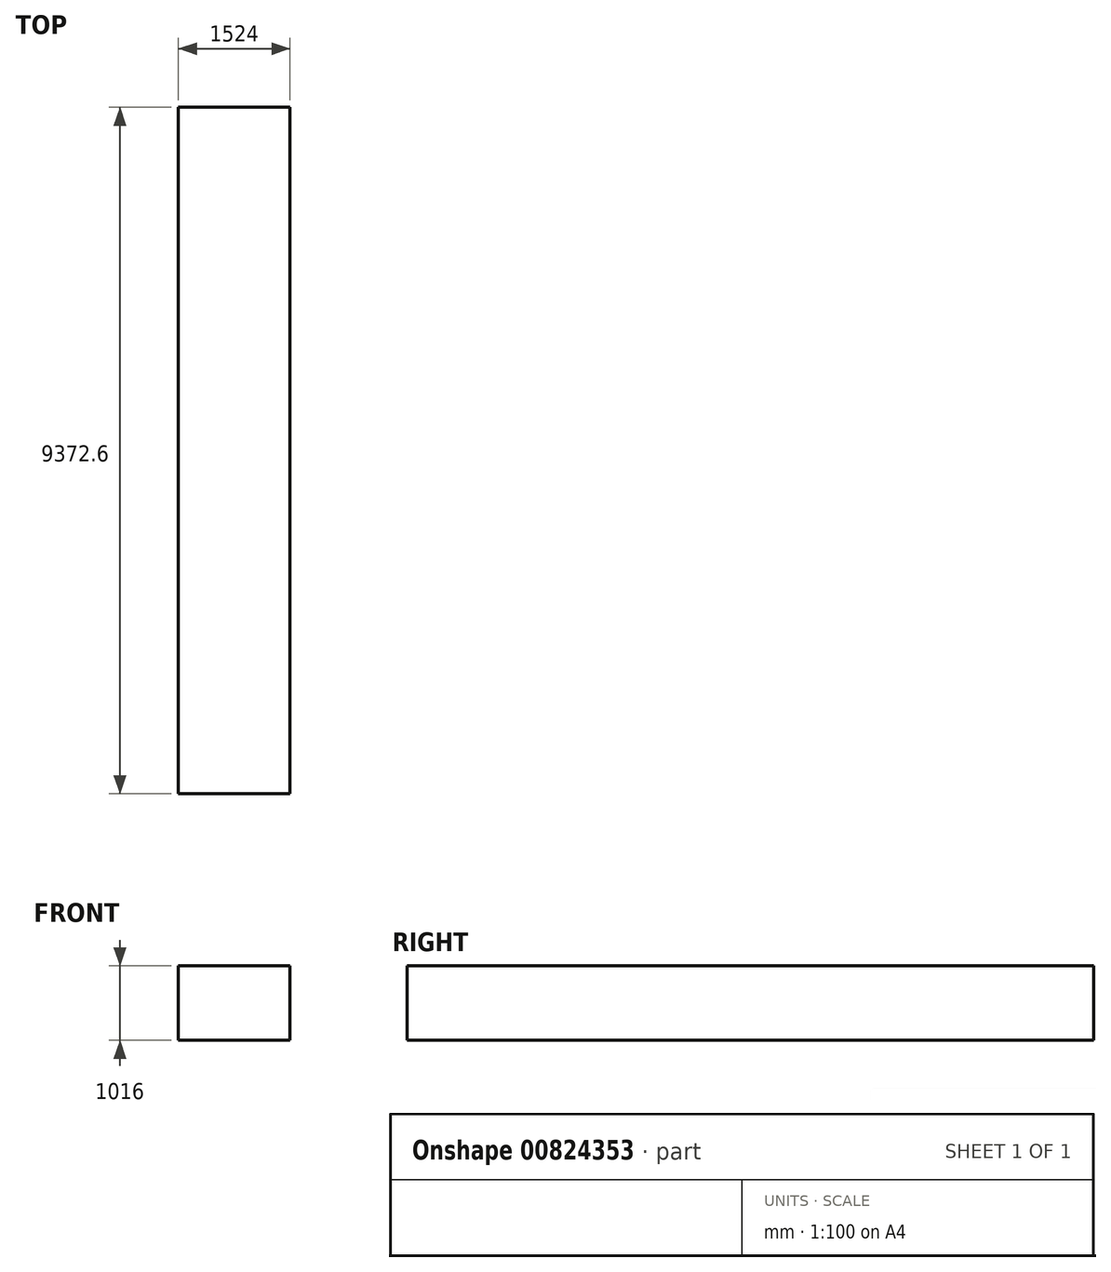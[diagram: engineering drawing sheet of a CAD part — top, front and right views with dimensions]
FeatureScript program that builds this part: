
annotation { "Feature Type Name" : "Feature", "Feature Type Description" : "" }
export const myFeature = defineFeature(function(context is Context, id is Id, definition is map)
    precondition{}
    {
        {
            var Q0;
            Q0=qCreatedBy(makeId("Front.planeOp"),FACE);
            var sketch = newSketch(context, id + "F0", { "sketchPlane" : qUnion([Q0])});
            skLineSegment(sketch, "E0.bottom", {"start": v(-762, 508) * mm, "end": v(762, 508) * mm});
            skLineSegment(sketch, "E0.top", {"start": v(-762, -508) * mm, "end": v(762, -508) * mm});
            skLineSegment(sketch, "E0.left", {"start": v(-762, 508) * mm, "end": v(-762, -508) * mm});
            skLineSegment(sketch, "E0.right", {"start": v(762, 508) * mm, "end": v(762, -508) * mm});
            skSolve(sketch);
        }
        {
            var Q0;
            Q0=makeQuery(id+"F0.imprint","IMPRINT",FACE,{"disambiguationData":[TD([[makeQuery(id+"F0.imprint","IMPRINT",EDGE,{"derivedFrom":sQuery(id+"F0.wireOp",EDGE,"E0.bottom")}),-1.0]])]});
            extrude(context, id + "F1", {"entities" : qUnion([Q0]), "endBound" : BoundingType.SYMMETRIC, "depth" : 9372.6 * mm, "offsetDistance" : 25.4 * mm});
        }
    });
